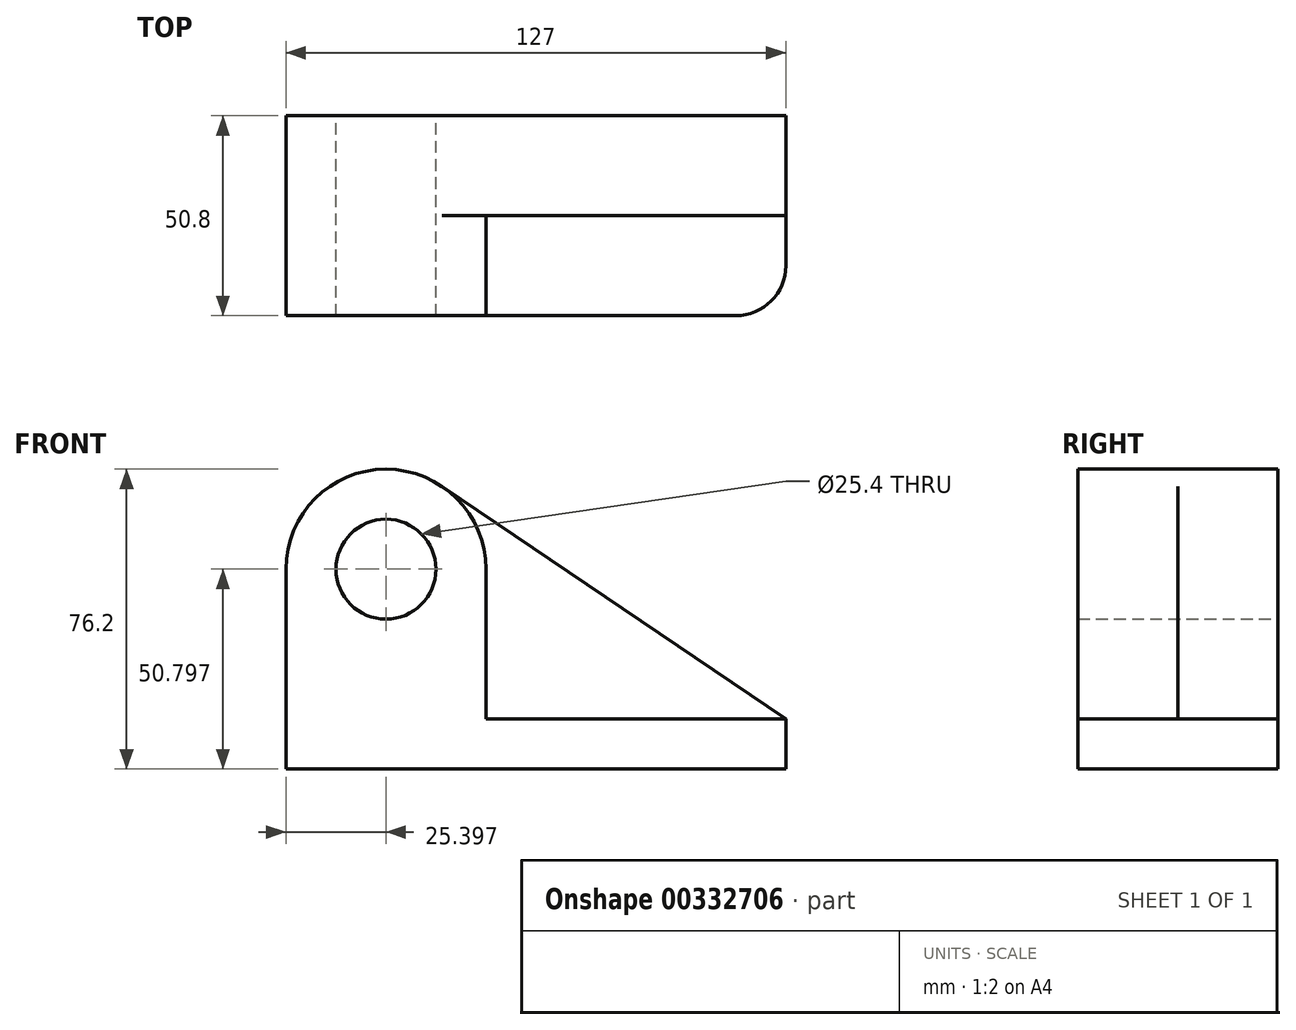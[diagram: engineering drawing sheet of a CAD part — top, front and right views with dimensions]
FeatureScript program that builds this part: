
annotation { "Feature Type Name" : "Feature", "Feature Type Description" : "" }
export const myFeature = defineFeature(function(context is Context, id is Id, definition is map)
    precondition{}
    {
        {
            var Q0;
            Q0=qCreatedBy(makeId("Front.planeOp"),FACE);
            var sketch = newSketch(context, id + "F0", { "sketchPlane" : qUnion([Q0])});
            skCircle(sketch, "E0", {"center": v(-40.84, 54) * mm, "radius": 12.7 * mm});
            skArc(sketch, "E1", {"start": v(-26.6, 75.03) * mm, "mid": v(-52.75, 76.43) * mm, "end": v(-66.24, 54) * mm});
            skLineSegment(sketch, "E2", {"start": v(-66.24, 54) * mm, "end": v(-66.24, 3.2) * mm});
            skLineSegment(sketch, "E3", {"start": v(-66.24, 3.2) * mm, "end": v(60.76, 3.2) * mm});
            skLineSegment(sketch, "E4", {"start": v(60.76, 3.2) * mm, "end": v(60.76, 15.9) * mm});
            skLineSegment(sketch, "E5", {"start": v(-26.6, 75.03) * mm, "end": v(-26.6, 79.11) * mm});
            skLineSegment(sketch, "E6", {"start": v(60.76, 15.9) * mm, "end": v(-26.6, 75.03) * mm});
            skSolve(sketch);
        }
        {
            var Q0;
            Q0 = qSketchRegion(id + "F0", true);
            extrude(context, id + "F1", {"entities" : qUnion([Q0]), "depth" : 25.4 * mm});
        }
        {
            var Q0;
            Q0=makeQuery(id+"F1.opExtrude","CAP_FACE",FACE,{"disambiguationData":[OSD([sQuery(id+"F0.wireOp",EDGE,"E0"),sQuery(id+"F0.wireOp",EDGE,"E1"),sQuery(id+"F0.wireOp",EDGE,"E2"),sQuery(id+"F0.wireOp",EDGE,"E3"),sQuery(id+"F0.wireOp",EDGE,"E4"),sQuery(id+"F0.wireOp",EDGE,"E6")])],"isStart":false});
            var sketch = newSketch(context, id + "F2", { "sketchPlane" : qUnion([Q0])});
            skCircle(sketch, "E7", {"center": v(-40.84, 54) * mm, "radius": 12.7 * mm});
            skArc(sketch, "E8", {"start": v(-15.44, 54) * mm, "mid": v(-40.84, 79.4) * mm, "end": v(-66.24, 54) * mm});
            skLineSegment(sketch, "E9.bottom", {"start": v(60.76, 15.9) * mm, "end": v(-15.44, 15.9) * mm});
            skLineSegment(sketch, "E9.top", {"start": v(60.76, 3.2) * mm, "end": v(-66.24, 3.2) * mm});
            skLineSegment(sketch, "E9.left", {"start": v(60.76, 15.9) * mm, "end": v(60.76, 3.2) * mm});
            skLineSegment(sketch, "E9.right", {"start": v(-66.24, 15.9) * mm, "end": v(-66.24, 3.2) * mm});
            skLineSegment(sketch, "E10", {"start": v(-15.44, 54) * mm, "end": v(-15.44, 15.9) * mm});
            skLineSegment(sketch, "E11", {"start": v(-66.24, 54) * mm, "end": v(-66.24, 3.2) * mm});
            skSolve(sketch);
        }
        {
            var Q0;
            Q0=makeQuery(id+"F2.imprint","IMPRINT",FACE,{"disambiguationData":[TD([[makeQuery(id+"F2.imprint","IMPRINT",EDGE,{"derivedFrom":sQuery(id+"F2.wireOp",EDGE,"E7")}),-1.0]])]});
            extrude(context, id + "F3", {"entities" : qUnion([Q0]), "operationType" : NewBodyOperationType.ADD, "depth" : 25.4 * mm});
        }
        {
            var Q0;
            Q0=makeQuery(id+"F3.opExtrude","CAP_EDGE",EDGE,{"disambiguationData":[OSD([sQuery(id+"F2.wireOp",EDGE,"E9.left")])],"isStart":false});
            fillet(context, id + "F4", {"entities" : qUnion([Q0]), "radius" : 12.7 * mm, "tangentPropagation" : true, "allowEdgeOverflow" : false});
        }
    });
